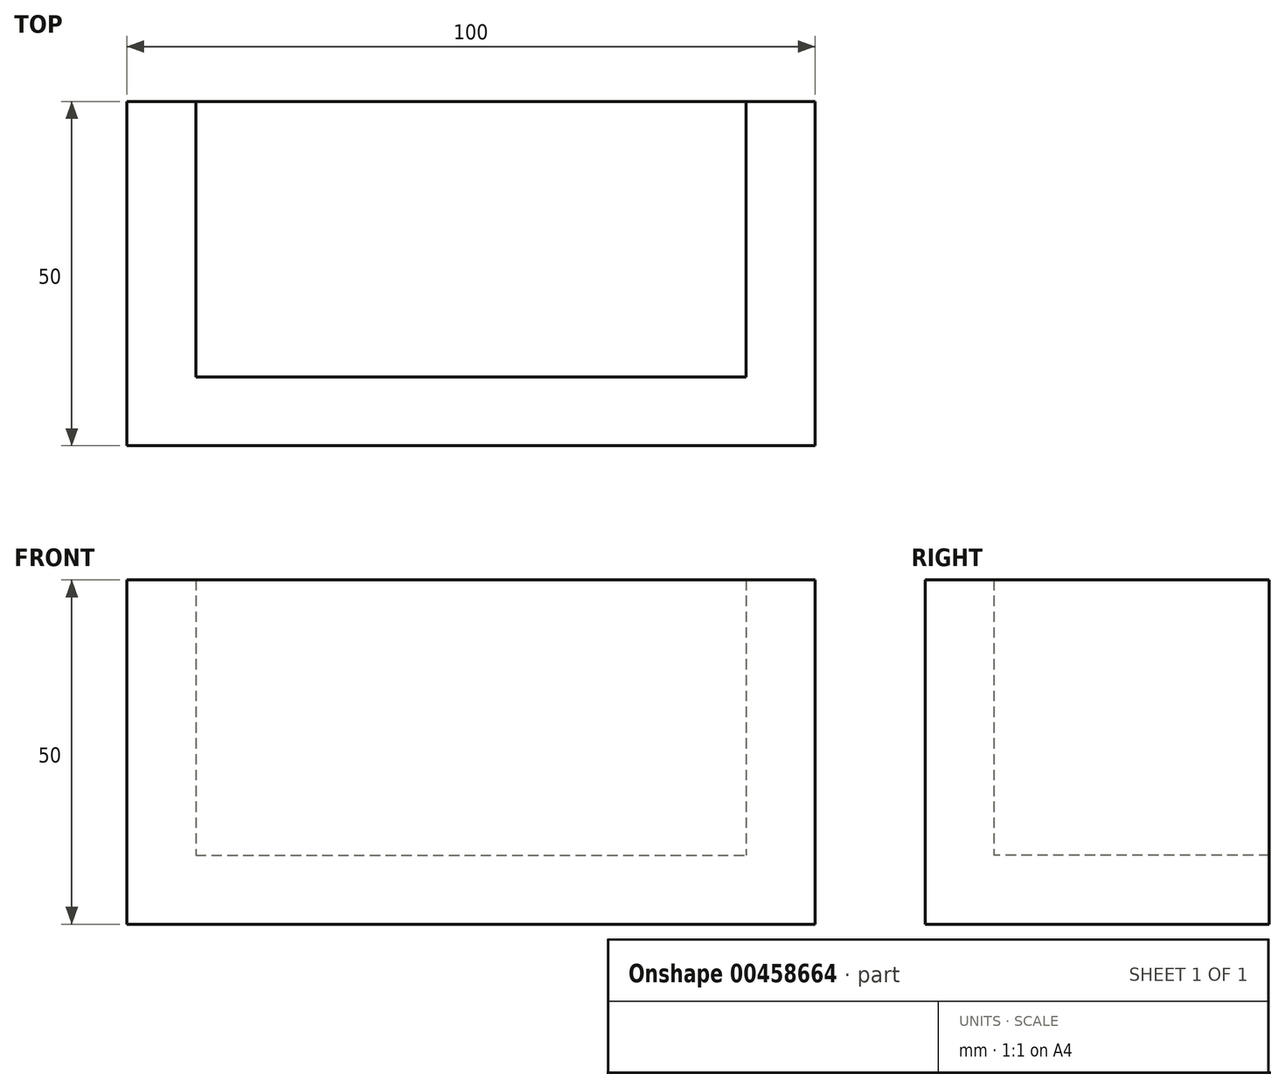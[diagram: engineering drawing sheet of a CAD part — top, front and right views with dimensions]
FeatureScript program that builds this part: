
annotation { "Feature Type Name" : "Feature", "Feature Type Description" : "" }
export const myFeature = defineFeature(function(context is Context, id is Id, definition is map)
    precondition{}
    {
        {
            var Q0;
            Q0=qCreatedBy(makeId("Top.planeOp"),FACE);
            var sketch = newSketch(context, id + "F0", { "sketchPlane" : qUnion([Q0])});
            skLineSegment(sketch, "E0.bottom", {"start": v(-50, 25) * mm, "end": v(50, 25) * mm});
            skLineSegment(sketch, "E0.top", {"start": v(-50, -25) * mm, "end": v(50, -25) * mm});
            skLineSegment(sketch, "E0.left", {"start": v(-50, 25) * mm, "end": v(-50, -25) * mm});
            skLineSegment(sketch, "E0.right", {"start": v(50, 25) * mm, "end": v(50, -25) * mm});
            skSolve(sketch);
        }
        {
            var Q0;
            Q0=makeQuery(id+"F0.imprint","IMPRINT",FACE,{"disambiguationData":[TD([[makeQuery(id+"F0.imprint","IMPRINT",EDGE,{"derivedFrom":sQuery(id+"F0.wireOp",EDGE,"E0.bottom")}),-1.0]])]});
            extrude(context, id + "F1", {"entities" : qUnion([Q0]), "depth" : 10 * mm});
        }
        {
            var Q0;
            Q0=makeQuery(id+"F1.opExtrude","CAP_FACE",FACE,{"disambiguationData":[OSD([sQuery(id+"F0.wireOp",EDGE,"E0.bottom"),sQuery(id+"F0.wireOp",EDGE,"E0.top"),sQuery(id+"F0.wireOp",EDGE,"E0.left"),sQuery(id+"F0.wireOp",EDGE,"E0.right")])],"isStart":false});
            var sketch = newSketch(context, id + "F2", { "sketchPlane" : qUnion([Q0])});
            skLineSegment(sketch, "E1", {"start": v(-50, 25) * mm, "end": v(-40, 25) * mm});
            skLineSegment(sketch, "E2", {"start": v(-40, 25) * mm, "end": v(-40, -15) * mm});
            skLineSegment(sketch, "E3", {"start": v(-40, -15) * mm, "end": v(40, -15) * mm});
            skLineSegment(sketch, "E4", {"start": v(40, -15) * mm, "end": v(40, 25) * mm});
            skLineSegment(sketch, "E5", {"start": v(40, 25) * mm, "end": v(50, 25) * mm});
            skLineSegment(sketch, "E6", {"start": v(50, 25) * mm, "end": v(50, -25) * mm});
            skLineSegment(sketch, "E7", {"start": v(50, -25) * mm, "end": v(-50, -25) * mm});
            skLineSegment(sketch, "E8", {"start": v(-50, -25) * mm, "end": v(-50, 25) * mm});
            skSolve(sketch);
        }
        {
            var Q0;
            Q0=makeQuery(id+"F2.imprint","IMPRINT",FACE,{"disambiguationData":[TD([[makeQuery(id+"F2.imprint","IMPRINT",EDGE,{"derivedFrom":sQuery(id+"F2.wireOp",EDGE,"E1")}),-1.0]])]});
            extrude(context, id + "F3", {"entities" : qUnion([Q0]), "operationType" : NewBodyOperationType.ADD, "depth" : 40 * mm});
        }
    });
